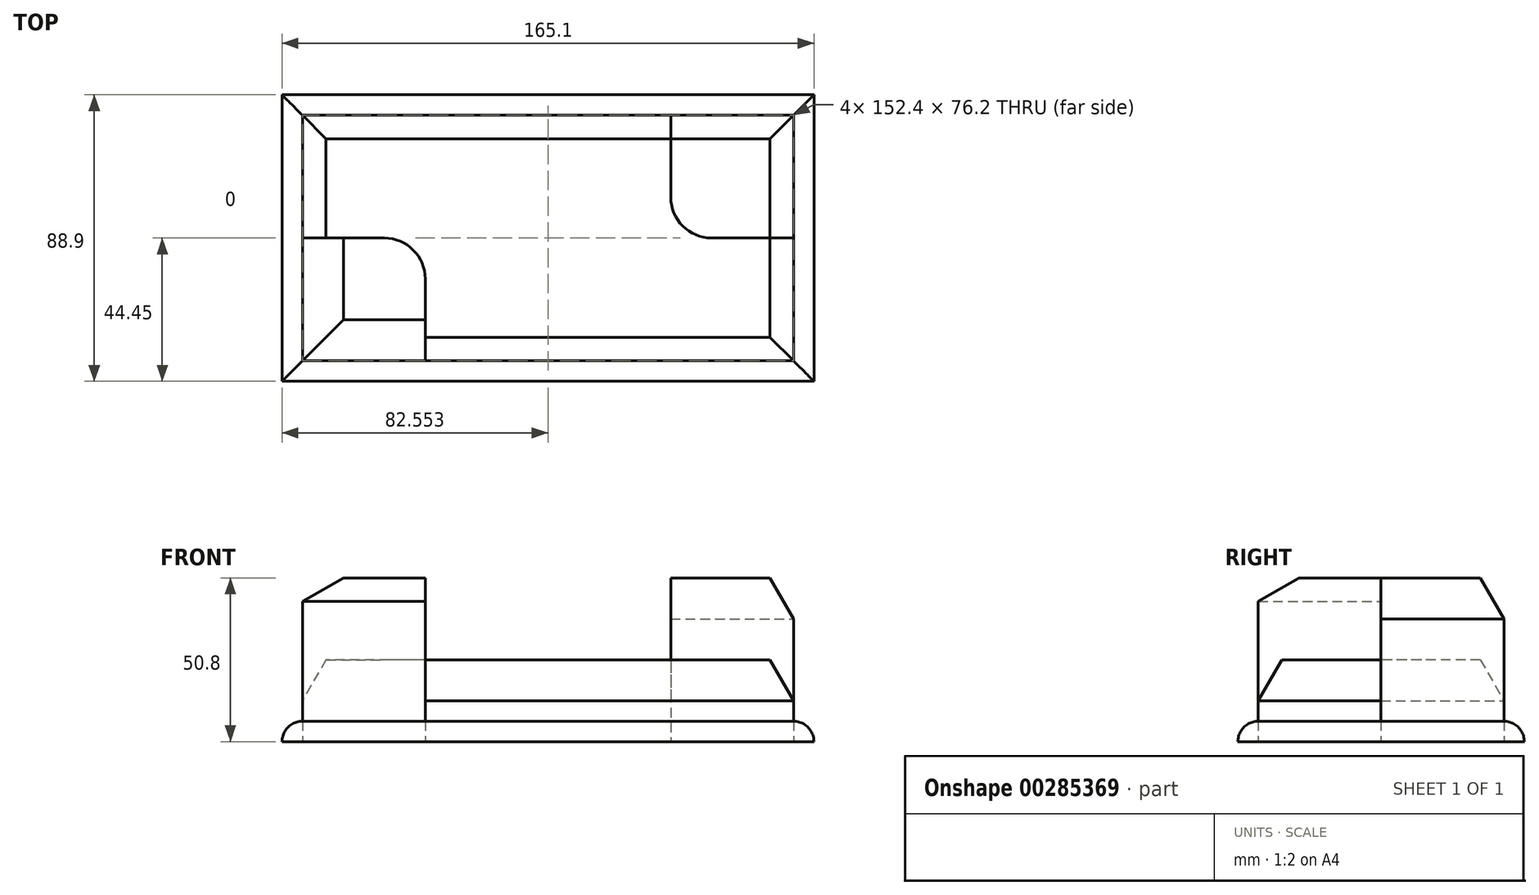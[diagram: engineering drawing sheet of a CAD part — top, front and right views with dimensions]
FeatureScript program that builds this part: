
annotation { "Feature Type Name" : "Feature", "Feature Type Description" : "" }
export const myFeature = defineFeature(function(context is Context, id is Id, definition is map)
    precondition{}
    {
        {
            var Q0;
            Q0=qCreatedBy(makeId("Top.planeOp"),FACE);
            var sketch = newSketch(context, id + "F0", { "sketchPlane" : qUnion([Q0])});
            skLineSegment(sketch, "E0.bottom", {"start": v(-74.45, 38.1) * mm, "end": v(77.95, 38.1) * mm});
            skLineSegment(sketch, "E0.top", {"start": v(-74.45, -38.1) * mm, "end": v(77.95, -38.1) * mm});
            skLineSegment(sketch, "E0.left", {"start": v(-74.45, 38.1) * mm, "end": v(-74.45, -38.1) * mm});
            skLineSegment(sketch, "E0.right", {"start": v(77.95, 38.1) * mm, "end": v(77.95, -38.1) * mm});
            skLineSegment(sketch, "E1", {"start": v(39.85, 38.1) * mm, "end": v(39.85, 12.7) * mm});
            skLineSegment(sketch, "E2", {"start": v(52.55, 0) * mm, "end": v(77.95, 0) * mm});
            skLineSegment(sketch, "E3", {"start": v(-74.45, 0) * mm, "end": v(-49.05, 0) * mm});
            skLineSegment(sketch, "E4", {"start": v(-36.35, -12.7) * mm, "end": v(-36.35, -38.1) * mm});
            skLineSegment(sketch, "E5.0", {"start": v(-80.8, 44.45) * mm, "end": v(84.3, 44.45) * mm});
            skLineSegment(sketch, "E5.1", {"start": v(-80.8, 44.45) * mm, "end": v(-80.8, -44.45) * mm});
            skLineSegment(sketch, "E5.2", {"start": v(-80.8, -44.45) * mm, "end": v(84.3, -44.45) * mm});
            skLineSegment(sketch, "E5.3", {"start": v(84.3, 44.45) * mm, "end": v(84.3, -44.45) * mm});
            skPoint(sketch, "E6.visualSharp", {"position": v(39.85, 0) * mm});
            skArc(sketch, "E6.filletArc", {"start": v(39.85, 12.7) * mm, "mid": v(43.57, 3.72) * mm, "end": v(52.55, 0) * mm});
            skPoint(sketch, "E7.visualSharp", {"position": v(-36.35, 0) * mm});
            skArc(sketch, "E7.filletArc", {"start": v(-36.35, -12.7) * mm, "mid": v(-40.07, -3.72) * mm, "end": v(-49.05, 0) * mm});
            skSolve(sketch);
        }
        {
            var Q0;
            {var subQ1=sQuery(id+"F0.wireOp",EDGE,"E3");Q0=makeQuery(id+"F0.imprint","IMPRINT",FACE,{"disambiguationData":[TD([[makeQuery(id+"F0.imprint","IMPRINT",EDGE,{"derivedFrom":subQ1}),-1.0]])]});}
            var Q1;
            {var subQ1=sQuery(id+"F0.wireOp",EDGE,"E1");Q1=makeQuery(id+"F0.imprint","IMPRINT",FACE,{"disambiguationData":[TD([[makeQuery(id+"F0.imprint","IMPRINT",EDGE,{"derivedFrom":subQ1}),1.0]])]});}
            extrude(context, id + "F1", {"entities" : qUnion([Q0, Q1]), "depth" : 50.8 * mm});
        }
        {
            var Q0;
            {var subQ9=sQuery(id+"F0.wireOp",EDGE,"E1");Q0=makeQuery(id+"F0.imprint","IMPRINT",FACE,{"disambiguationData":[TD([[makeQuery(id+"F0.imprint","IMPRINT",EDGE,{"derivedFrom":subQ9}),-1.0]])]});}
            extrude(context, id + "F2", {"entities" : qUnion([Q0]), "depth" : 25.4 * mm});
        }
        {
            var Q0;
            Q0=makeQuery(id+"F0.imprint","IMPRINT",FACE,{"disambiguationData":[TD([[makeQuery(id+"F0.imprint","IMPRINT",EDGE,{"derivedFrom":sQuery(id+"F0.wireOp",EDGE,"E5.0")}),-1.0]])]});
            extrude(context, id + "F3", {"entities" : qUnion([Q0]), "depth" : 6.35 * mm});
        }
        {
            var Q0;
            Q0=makeQuery(id+"F3.opExtrude","CAP_EDGE",EDGE,{"disambiguationData":[OSD([sQuery(id+"F0.wireOp",EDGE,"E5.2")])],"isStart":false});
            var Q1;
            Q1=makeQuery(id+"F3.opExtrude","CAP_EDGE",EDGE,{"disambiguationData":[OSD([sQuery(id+"F0.wireOp",EDGE,"E5.1")])],"isStart":false});
            var Q2;
            Q2=makeQuery(id+"F3.opExtrude","CAP_EDGE",EDGE,{"disambiguationData":[OSD([sQuery(id+"F0.wireOp",EDGE,"E5.0")])],"isStart":false});
            var Q3;
            Q3=makeQuery(id+"F3.opExtrude","CAP_EDGE",EDGE,{"disambiguationData":[OSD([sQuery(id+"F0.wireOp",EDGE,"E5.3")])],"isStart":false});
            fillet(context, id + "F4", {"entities" : qUnion([Q0, Q1, Q2, Q3]), "radius" : 6.35 * mm, "tangentPropagation" : true, "allowEdgeOverflow" : false});
        }
        {
            var Q0;
            Q0=makeQuery(id+"F1.opExtrude","CAP_EDGE",EDGE,{"disambiguationData":[OSD([sQuery(id+"F0.wireOp",EDGE,"E0.top")])],"isStart":false});
            var Q1;
            Q1=makeQuery(id+"F1.opExtrude","CAP_EDGE",EDGE,{"disambiguationData":[OSD([sQuery(id+"F0.wireOp",EDGE,"E0.left")])],"isStart":false});
            var Q2;
            Q2=makeQuery(id+"F1.opExtrude","CAP_EDGE",EDGE,{"disambiguationData":[OSD([sQuery(id+"F0.wireOp",EDGE,"E0.right")])],"isStart":false});
            var Q3;
            Q3=makeQuery(id+"F1.opExtrude","CAP_EDGE",EDGE,{"disambiguationData":[OSD([sQuery(id+"F0.wireOp",EDGE,"E0.bottom")])],"isStart":false});
            chamfer(context, id + "F5", {"entities" : qUnion([Q0, Q1, Q2, Q3]), "chamferType" : ChamferType.OFFSET_ANGLE, "width" : 12.7 * mm, "oppositeDirection" : false, "angle" : 30 * degree, "tangentPropagation" : true});
        }
        {
            var Q0;
            Q0=makeQuery(id+"F2.opExtrude","CAP_EDGE",EDGE,{"disambiguationData":[OSD([sQuery(id+"F0.wireOp",EDGE,"E0.bottom")])],"isStart":false});
            var Q1;
            Q1=makeQuery(id+"F2.opExtrude","CAP_EDGE",EDGE,{"disambiguationData":[OSD([sQuery(id+"F0.wireOp",EDGE,"E0.left")])],"isStart":false});
            var Q2;
            Q2=makeQuery(id+"F2.opExtrude","CAP_EDGE",EDGE,{"disambiguationData":[OSD([sQuery(id+"F0.wireOp",EDGE,"E0.top")])],"isStart":false});
            var Q3;
            Q3=makeQuery(id+"F2.opExtrude","CAP_EDGE",EDGE,{"disambiguationData":[OSD([sQuery(id+"F0.wireOp",EDGE,"E0.right")])],"isStart":false});
            chamfer(context, id + "F6", {"entities" : qUnion([Q0, Q1, Q2, Q3]), "chamferType" : ChamferType.OFFSET_ANGLE, "width" : 12.7 * mm, "oppositeDirection" : false, "angle" : 30 * degree, "tangentPropagation" : true});
        }
    });
